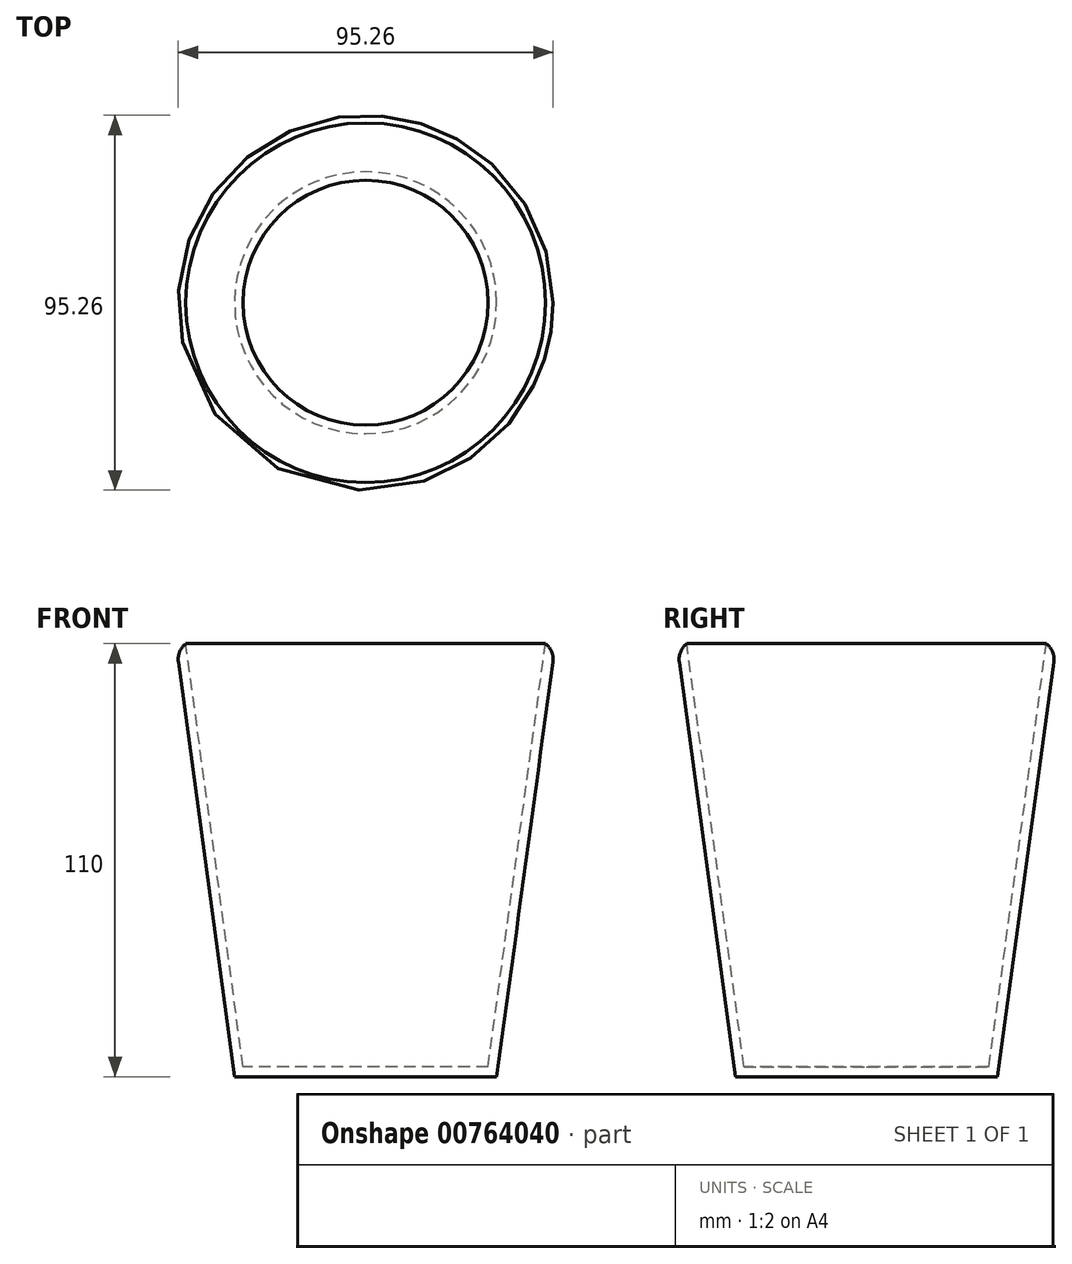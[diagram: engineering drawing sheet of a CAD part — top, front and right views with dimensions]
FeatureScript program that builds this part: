
annotation { "Feature Type Name" : "Feature", "Feature Type Description" : "" }
export const myFeature = defineFeature(function(context is Context, id is Id, definition is map)
    precondition{}
    {
        {
            var Q0;
            Q0=qCreatedBy(makeId("Top.planeOp"),FACE);
            cPlane(context, id + "F0", {"entities" : qUnion([Q0]), "cplaneType" : CPlaneType.OFFSET, "offset" : 110 * mm, "width" : 152.4 * mm, "height" : 152.4 * mm});
        }
        {
            var Q0;
            Q0=qCreatedBy(makeId("Top.planeOp"),FACE);
            var sketch = newSketch(context, id + "F1", { "sketchPlane" : qUnion([Q0])});
            skCircle(sketch, "E0", {"center": v(0, 0) * mm, "radius": 29.5 * mm});
            skSolve(sketch);
        }
        {
            var Q0;
            Q0=qCreatedBy(id+"F0.planeOp",FACE);
            var sketch = newSketch(context, id + "F2", { "sketchPlane" : qUnion([Q0])});
            skCircle(sketch, "E1", {"center": v(0, 0) * mm, "radius": 44.5 * mm});
            skSolve(sketch);
        }
        {
            var Q0;
            Q0=qCreatedBy(id+"F0.planeOp",FACE);
            var sketch = newSketch(context, id + "F3", { "sketchPlane" : qUnion([Q0])});
            skCircle(sketch, "E2", {"center": v(0, 0) * mm, "radius": 48.21 * mm});
            skSolve(sketch);
        }
        {
            var Q0;
            Q0=qCreatedBy(makeId("Top.planeOp"),FACE);
            var sketch = newSketch(context, id + "F4", { "sketchPlane" : qUnion([Q0])});
            skCircle(sketch, "E3", {"center": v(0, 0) * mm, "radius": 33.3 * mm});
            skSolve(sketch);
        }
        {
            var Q0;
            Q0=makeQuery(id+"F1.imprint","IMPRINT",FACE,{"disambiguationData":[TD([[makeQuery(id+"F1.imprint","IMPRINT",EDGE,{"derivedFrom":sQuery(id+"F1.wireOp",EDGE,"E0")}),1.0]])]});
            var Q1;
            Q1=makeQuery(id+"F2.imprint","IMPRINT",FACE,{"disambiguationData":[TD([[makeQuery(id+"F2.imprint","IMPRINT",EDGE,{"derivedFrom":sQuery(id+"F2.wireOp",EDGE,"E1")}),1.0]])]});
            loft(context, id + "F5", {"sheetProfilesArray" : [{ "sheetProfileEntities" : qUnion([Q0]) }, { "sheetProfileEntities" : qUnion([Q1]) }]});
        }
        {
            var Q1;
            Q1=makeQuery(id+"F3.imprint","IMPRINT",FACE,{"disambiguationData":[TD([[makeQuery(id+"F3.imprint","IMPRINT",EDGE,{"derivedFrom":sQuery(id+"F3.wireOp",EDGE,"E2")}),1.0]])]});
            var Q2;
            Q2=makeQuery(id+"F4.imprint","IMPRINT",FACE,{"disambiguationData":[TD([[makeQuery(id+"F4.imprint","IMPRINT",EDGE,{"derivedFrom":sQuery(id+"F4.wireOp",EDGE,"E3")}),1.0]])]});
            loft(context, id + "F6", {"sheetProfilesArray" : [{ "sheetProfileEntities" : qUnion([Q1]) }, { "sheetProfileEntities" : qUnion([Q2]) }]});
        }
        {
            var Q0;
            Q0=makeQuery(id+"F5.opLoft","SWEPT_BODY",BODY,{"disambiguationData":[OSD([makeQuery(id+"F1.imprint","IMPRINT",FACE,{"disambiguationData":[TD([[makeQuery(id+"F1.imprint","IMPRINT",EDGE,{"derivedFrom":sQuery(id+"F1.wireOp",EDGE,"E0")}),1.0]])]}),makeQuery(id+"F2.imprint","IMPRINT",FACE,{"disambiguationData":[TD([[makeQuery(id+"F2.imprint","IMPRINT",EDGE,{"derivedFrom":sQuery(id+"F2.wireOp",EDGE,"E1")}),1.0]])]})])]});
            deleteBodies(context, id + "F7", {"entities" : qUnion([Q0])});
        }
        {
            var Q0;
            Q0=makeQuery(id+"F6.opLoft","CAP_FACE",FACE,{"disambiguationData":[OSD([makeQuery(id+"F3.imprint","IMPRINT",FACE,{"disambiguationData":[TD([[makeQuery(id+"F3.imprint","IMPRINT",EDGE,{"derivedFrom":sQuery(id+"F3.wireOp",EDGE,"E2")}),1.0]])]})])],"isStart":true});
            shell(context, id + "F8", {"entities" : qUnion([Q0]), "thickness" : 2.5 * mm});
        }
        {
            var Q0;
            Q0=makeQuery(id+"F6.opLoft","MID_CAP_EDGE",EDGE,{"disambiguationData":[OSD([sQuery(id+"F3.wireOp",EDGE,"E2")])],"capPos":0.0});
            fillet(context, id + "F9", {"entities" : qUnion([Q0]), "radius" : 5 * mm, "tangentPropagation" : true, "allowEdgeOverflow" : false});
        }
    });
